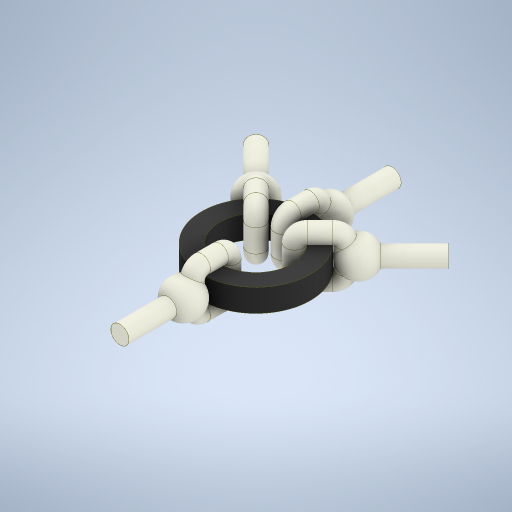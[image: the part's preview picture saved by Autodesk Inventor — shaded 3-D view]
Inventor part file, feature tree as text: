
AUTODESK INVENTOR PART (.ipt)
format: ipt  version: 2024.3 (Build 283343000, 343)  size: 464,896 bytes
history: native  units: mm
features: sketch x5, extrude x3, sweep x2, revolve x2, plane x2, pattern_circular x2, other x1, projected_geometry x1
ambient origin geometry x8: Origin, YZ Plane, XZ Plane, XY Plane, X Axis, Y Axis, Z Axis, Center Point
bodies: Body1 (feature_tree)
feature tree (18):
  other  "솔리드1"
  extrude  "돌출1"  Depth=4.8mm
  sketch  "Sketch2"  dims[d0=3.2mm d1=4.8mm]
  sketch  "Sketch3"  dims[d2=1.0mm d3=0.0mm d4=0.5mm]
  sweep  "Sweep1"
  sweep  "Sweep2"
  revolve  "Revolution1"  [1 undecoded]
  revolve  "Revolution2"  [1 undecoded]
  plane  "Work Plane2"
  extrude  "Extrusion2"  Depth=0.8mm
  extrude  "Extrusion3"  TaperAngle=0.0deg  [1 undecoded]
  pattern_circular  "Circular Pattern1"  [2 undecoded]
  pattern_circular  "Circular Pattern2"  [2 undecoded]
  sketch  "스케치1"
  plane  "Work Plane1"
  sketch  "Sketch5"  dims[d8=0.4mm d9=0.4mm]
  projected_geometry  "Projected Loop1"
  sketch  "Sketch6"  dims[d10=0.4mm d12=0.78mm d13=0.0mm d14=0.0mm d15=0.78mm d16=0.0mm d17=0.0mm d20=1.6mm d21=0.8mm d22=1.6mm d23=0.8mm d24=90.0deg d25=90.0deg d27=0.8mm d28=2.0mm d29=1.0mm d30=0.0mm d31=0.0mm d32=0.8mm d33=0.5mm d34=2.0mm d35=0.0mm d36=0.0mm d37=20.0mm d38=45.0deg d40=20.0mm d41=45.0deg]
note: 7 required parameter values undecoded (feature->parameter linkage not recoverable at this tier; creation-order binding heuristic only, values carry confidence <= 0.55)